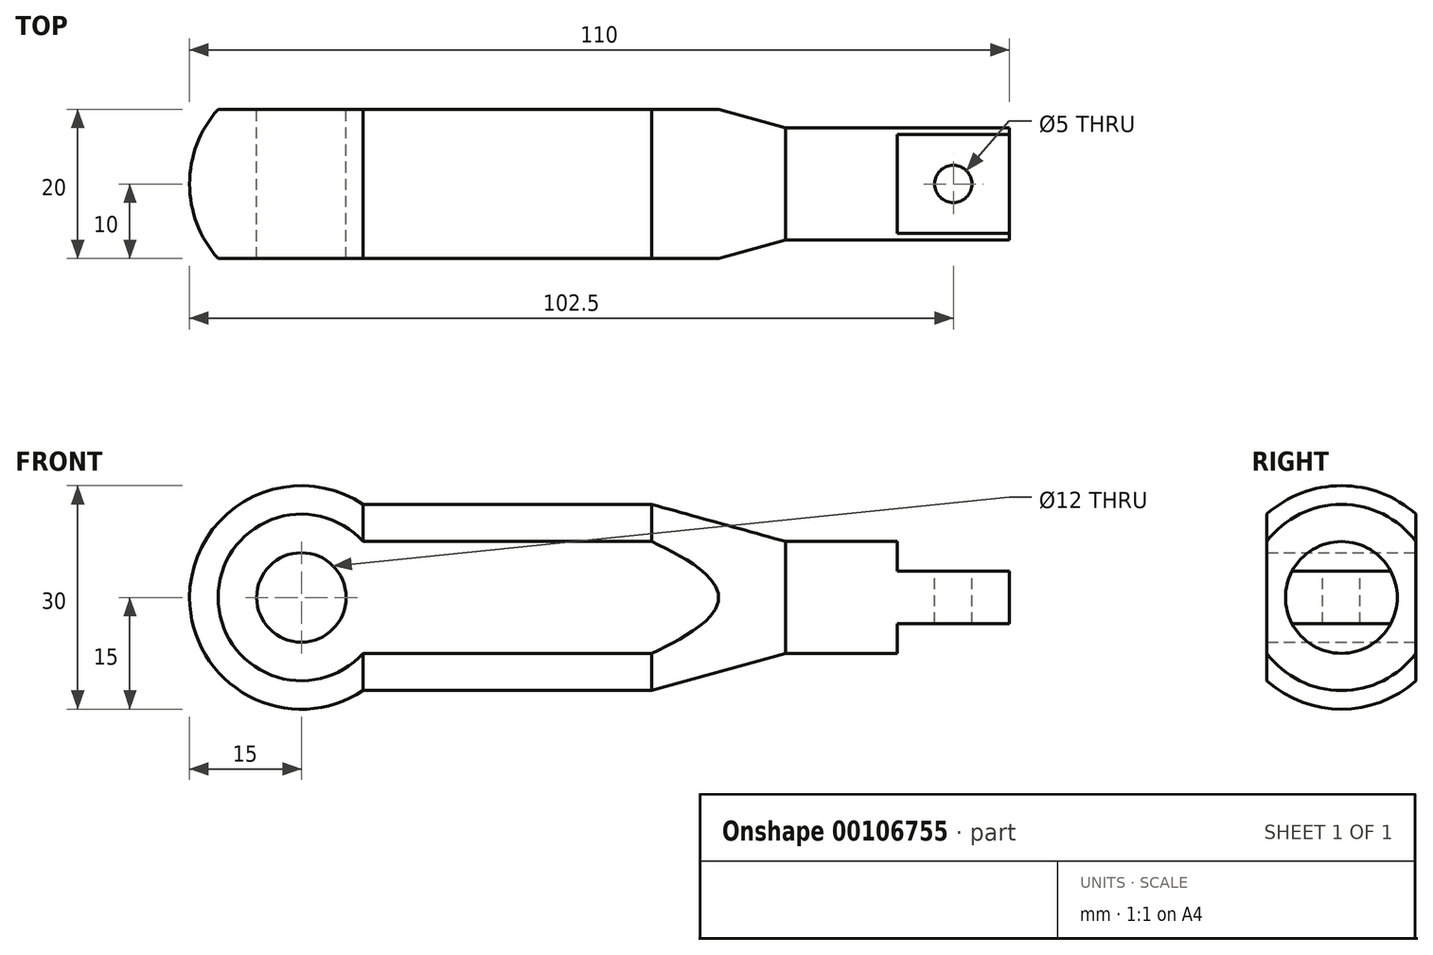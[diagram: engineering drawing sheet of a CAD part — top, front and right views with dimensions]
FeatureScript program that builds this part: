
annotation { "Feature Type Name" : "Feature", "Feature Type Description" : "" }
export const myFeature = defineFeature(function(context is Context, id is Id, definition is map)
    precondition{}
    {
        {
            var Q0;
            Q0=qCreatedBy(makeId("Front.planeOp"),FACE);
            var sketch = newSketch(context, id + "F0", { "sketchPlane" : qUnion([Q0])});
            skLineSegment(sketch, "E0", {"start": v(0, 0) * mm, "end": v(95, 0) * mm, "construction": true});
            skLineSegment(sketch, "E1.bottom", {"start": v(95, 0) * mm, "end": v(65, 0) * mm});
            skLineSegment(sketch, "E1.top", {"start": v(95, 7.5) * mm, "end": v(65, 7.5) * mm});
            skLineSegment(sketch, "E1.left", {"start": v(95, 0) * mm, "end": v(95, 7.5) * mm});
            skLineSegment(sketch, "E1.right", {"start": v(65, 0) * mm, "end": v(65, 7.5) * mm});
            skLineSegment(sketch, "E2.bottom", {"start": v(8.3, 12.5) * mm, "end": v(47, 12.5) * mm});
            skLineSegment(sketch, "E2.top", {"start": v(8.3, 0) * mm, "end": v(47, 0) * mm});
            skLineSegment(sketch, "E2.left", {"start": v(8.3, 12.5) * mm, "end": v(8.3, 0) * mm});
            skLineSegment(sketch, "E2.right", {"start": v(47, 12.5) * mm, "end": v(47, 0) * mm});
            skArc(sketch, "E3", {"start": v(8.3, 12.5) * mm, "mid": v(-7.1, 13.22) * mm, "end": v(-15, 0) * mm});
            skLineSegment(sketch, "E4", {"start": v(47, 12.5) * mm, "end": v(65, 7.5) * mm});
            skLineSegment(sketch, "E5", {"start": v(47, 0) * mm, "end": v(65, 0) * mm});
            skLineSegment(sketch, "E6", {"start": v(-15, 0) * mm, "end": v(8.3, 0) * mm});
            skSolve(sketch);
        }
        {
            var Q0;
            Q0=makeQuery(id+"F0.imprint","IMPRINT",FACE,{"disambiguationData":[TD([[makeQuery(id+"F0.imprint","IMPRINT",EDGE,{"derivedFrom":sQuery(id+"F0.wireOp",EDGE,"E2.left")}),-1.0]])]});
            var Q1;
            Q1=makeQuery(id+"F0.imprint","IMPRINT",FACE,{"disambiguationData":[TD([[makeQuery(id+"F0.imprint","IMPRINT",EDGE,{"derivedFrom":sQuery(id+"F0.wireOp",EDGE,"E2.bottom")}),-1.0]])]});
            var Q2;
            Q2=makeQuery(id+"F0.imprint","IMPRINT",FACE,{"disambiguationData":[TD([[makeQuery(id+"F0.imprint","IMPRINT",EDGE,{"derivedFrom":sQuery(id+"F0.wireOp",EDGE,"E1.right")}),1.0]])]});
            var Q3;
            Q3=makeQuery(id+"F0.imprint","IMPRINT",FACE,{"disambiguationData":[TD([[makeQuery(id+"F0.imprint","IMPRINT",EDGE,{"derivedFrom":sQuery(id+"F0.wireOp",EDGE,"E1.bottom")}),-1.0]])]});
            var Q4;
            Q4=sQuery(id+"F0.wireOp",EDGE,"E2.top");
            revolve(context, id + "F1", {"entities" : qUnion([Q0, Q1, Q2, Q3]), "axis" : qUnion([Q4]), "revolveType" : RevolveType.FULL});
        }
        {
            var Q0;
            Q0=qCreatedBy(makeId("Front.planeOp"),FACE);
            var sketch = newSketch(context, id + "F2", { "sketchPlane" : qUnion([Q0])});
            skLineSegment(sketch, "E7", {"start": v(76.62, 0) * mm, "end": v(119.25, 0) * mm, "construction": true});
            skLineSegment(sketch, "E8", {"start": v(80, 15.81) * mm, "end": v(80, 8.95) * mm, "construction": true});
            skLineSegment(sketch, "E9", {"start": v(80, 3.5) * mm, "end": v(96.98, 3.5) * mm, "construction": true});
            skLineSegment(sketch, "E10.bottom", {"start": v(80, 3.5) * mm, "end": v(95, 3.5) * mm});
            skLineSegment(sketch, "E10.left", {"start": v(80, 3.5) * mm, "end": v(80, 7.5) * mm});
            skLineSegment(sketch, "E10.right", {"start": v(95, 3.5) * mm, "end": v(95, 7.5) * mm});
            skLineSegment(sketch, "E11", {"start": v(80, 7.5) * mm, "end": v(95, 7.5) * mm});
            skLineSegment(sketch, "E12.trimOffspring", {"start": v(80, 7.5) * mm, "end": v(80, -16.58) * mm, "construction": true});
            skLineSegment(sketch, "E13.MirrorCS", {"start": v(80, -7.5) * mm, "end": v(95, -7.5) * mm});
            skLineSegment(sketch, "E14.MirrorCS", {"start": v(95, -3.5) * mm, "end": v(95, -7.5) * mm});
            skLineSegment(sketch, "E15.MirrorCS", {"start": v(80, -3.5) * mm, "end": v(96.98, -3.5) * mm, "construction": true});
            skLineSegment(sketch, "E16.MirrorCS", {"start": v(80, -7.5) * mm, "end": v(80, 16.58) * mm, "construction": true});
            skLineSegment(sketch, "E17", {"start": v(95, -3.5) * mm, "end": v(80, -3.5) * mm});
            skLineSegment(sketch, "E18", {"start": v(80, -7.5) * mm, "end": v(80, -3.5) * mm});
            skSolve(sketch);
        }
        {
            var Q0;
            Q0 = qSketchRegion(id + "F2", true);
            extrude(context, id + "F3", {"entities" : qUnion([Q0]), "operationType" : NewBodyOperationType.REMOVE, "endBound" : BoundingType.THROUGH_ALL, "oppositeDirection" : true, "depth" : 25 * mm, "hasSecondDirection" : true, "secondDirectionBound" : SecondDirectionBoundingType.THROUGH_ALL, "secondDirectionOppositeDirection" : false, "secondDirectionDepth" : 25 * mm});
        }
        {
            var Q0;
            Q0=makeQuery(id+"F3.boolean.opBoolean","COPY",FACE,{"derivedFrom":makeQuery(id+"F3.opExtrude","SWEPT_FACE",FACE,{"disambiguationData":[OSD([sQuery(id+"F2.wireOp",EDGE,"E10.bottom")])]})});
            var sketch = newSketch(context, id + "F4", { "sketchPlane" : qUnion([Q0])});
            skCircle(sketch, "E19", {"center": v(87.5, 0) * mm, "radius": 2.5 * mm});
            skSolve(sketch);
        }
        {
            var Q0;
            Q0 = qSketchRegion(id + "F4", true);
            extrude(context, id + "F5", {"entities" : qUnion([Q0]), "operationType" : NewBodyOperationType.REMOVE, "endBound" : BoundingType.THROUGH_ALL, "oppositeDirection" : true, "depth" : 25 * mm});
        }
        {
            var Q0;
            Q0=qCreatedBy(makeId("Front.planeOp"),FACE);
            var sketch = newSketch(context, id + "F6", { "sketchPlane" : qUnion([Q0])});
            skCircle(sketch, "E20", {"center": v(0, 0) * mm, "radius": 6 * mm});
            skSolve(sketch);
        }
        {
            var Q0;
            Q0=qCreatedBy(makeId("Right.planeOp"),FACE);
            var sketch = newSketch(context, id + "F7", { "sketchPlane" : qUnion([Q0])});
            skLineSegment(sketch, "E21", {"start": v(-10, -11.18) * mm, "end": v(-10, 11.18) * mm, "construction": true});
            skLineSegment(sketch, "E22", {"start": v(10, 11.18) * mm, "end": v(10, -11.18) * mm, "construction": true});
            skLineSegment(sketch, "E23", {"start": v(10, 11.18) * mm, "end": v(10, -11.18) * mm});
            skLineSegment(sketch, "E24", {"start": v(-10, 11.18) * mm, "end": v(-10, -11.18) * mm});
            skArc(sketch, "E25", {"start": v(-10, 11.18) * mm, "mid": v(-15, 0) * mm, "end": v(-10, -11.18) * mm});
            skPoint(sketch, "E26.orphan", {"position": v(-10, 24.88) * mm});
            skPoint(sketch, "E27.orphan", {"position": v(10, 24.88) * mm});
            skArc(sketch, "E28.trimOffspring", {"start": v(10, -11.18) * mm, "mid": v(15, 0) * mm, "end": v(10, 11.18) * mm});
            skSolve(sketch);
        }
        {
            var Q0;
            Q0 = qSketchRegion(id + "F7", true);
            extrude(context, id + "F8", {"entities" : qUnion([Q0]), "operationType" : NewBodyOperationType.REMOVE, "endBound" : BoundingType.THROUGH_ALL, "oppositeDirection" : true, "depth" : 25 * mm});
        }
        {
            var Q0;
            Q0 = qSketchRegion(id + "F7", true);
            extrude(context, id + "F9", {"entities" : qUnion([Q0]), "operationType" : NewBodyOperationType.REMOVE, "endBound" : BoundingType.THROUGH_ALL, "oppositeDirection" : true, "depth" : 25 * mm, "hasSecondDirection" : true, "secondDirectionBound" : SecondDirectionBoundingType.THROUGH_ALL, "secondDirectionOppositeDirection" : false, "secondDirectionDepth" : 25 * mm});
        }
        {
            var Q0;
            Q0 = qSketchRegion(id + "F6", true);
            extrude(context, id + "F10", {"entities" : qUnion([Q0]), "operationType" : NewBodyOperationType.REMOVE, "endBound" : BoundingType.THROUGH_ALL, "depth" : 25 * mm, "hasSecondDirection" : true, "secondDirectionBound" : SecondDirectionBoundingType.THROUGH_ALL, "secondDirectionOppositeDirection" : true, "secondDirectionDepth" : 25 * mm});
        }
        {
            var Q0;
            Q0 = qSketchRegion(id + "F6", true);
            extrude(context, id + "F11", {"entities" : qUnion([Q0]), "operationType" : NewBodyOperationType.REMOVE, "endBound" : BoundingType.SYMMETRIC, "oppositeDirection" : true, "depth" : 500 * mm});
        }
    });
